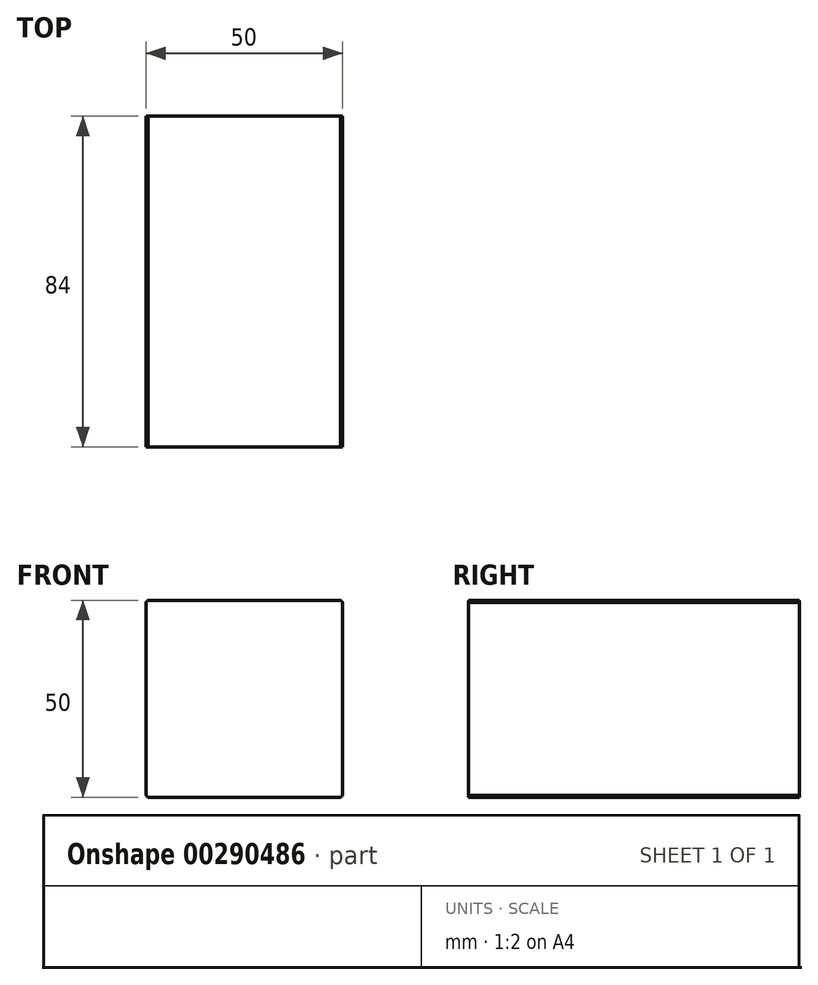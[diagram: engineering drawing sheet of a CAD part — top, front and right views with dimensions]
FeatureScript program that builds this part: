
annotation { "Feature Type Name" : "Feature", "Feature Type Description" : "" }
export const myFeature = defineFeature(function(context is Context, id is Id, definition is map)
    precondition{}
    {
        {
            var Q0;
            Q0=qCreatedBy(makeId("Front.planeOp"),FACE);
            var sketch = newSketch(context, id + "F0", { "sketchPlane" : qUnion([Q0])});
            skArc(sketch, "E0", {"start": v(-24.5, 25) * mm, "mid": v(-24.75, 24.75) * mm, "end": v(-25, 24.5) * mm});
            skLineSegment(sketch, "E1.bottom", {"start": v(24.5, 25) * mm, "end": v(-24.5, 25) * mm});
            skLineSegment(sketch, "E1.top", {"start": v(24.5, -25) * mm, "end": v(-24.5, -25) * mm});
            skLineSegment(sketch, "E1.left", {"start": v(25, 24.5) * mm, "end": v(25, -24.5) * mm});
            skLineSegment(sketch, "E1.right", {"start": v(-25, 24.5) * mm, "end": v(-25, -24.5) * mm});
            skPoint(sketch, "E2.orphan", {"position": v(-25, 25) * mm});
            skArc(sketch, "E3.trimOffspring", {"start": v(-25, -24.5) * mm, "mid": v(-24.75, -24.75) * mm, "end": v(-24.5, -25) * mm});
            skPoint(sketch, "E4.orphan", {"position": v(25, 25) * mm});
            skArc(sketch, "E5.trimOffspring", {"start": v(25, 24.5) * mm, "mid": v(24.75, 24.75) * mm, "end": v(24.5, 25) * mm});
            skArc(sketch, "E6.trimOffspring", {"start": v(24.5, -25) * mm, "mid": v(24.75, -24.75) * mm, "end": v(25, -24.5) * mm});
            skPoint(sketch, "E7.orphan", {"position": v(25, -25) * mm});
            skPoint(sketch, "E8.orphan", {"position": v(-25, -25) * mm});
            skSolve(sketch);
        }
        {
            var Q0;
            Q0 = qSketchRegion(id + "F0", true);
            extrude(context, id + "F1", {"entities" : qUnion([Q0]), "depth" : 84 * mm});
        }
    });
